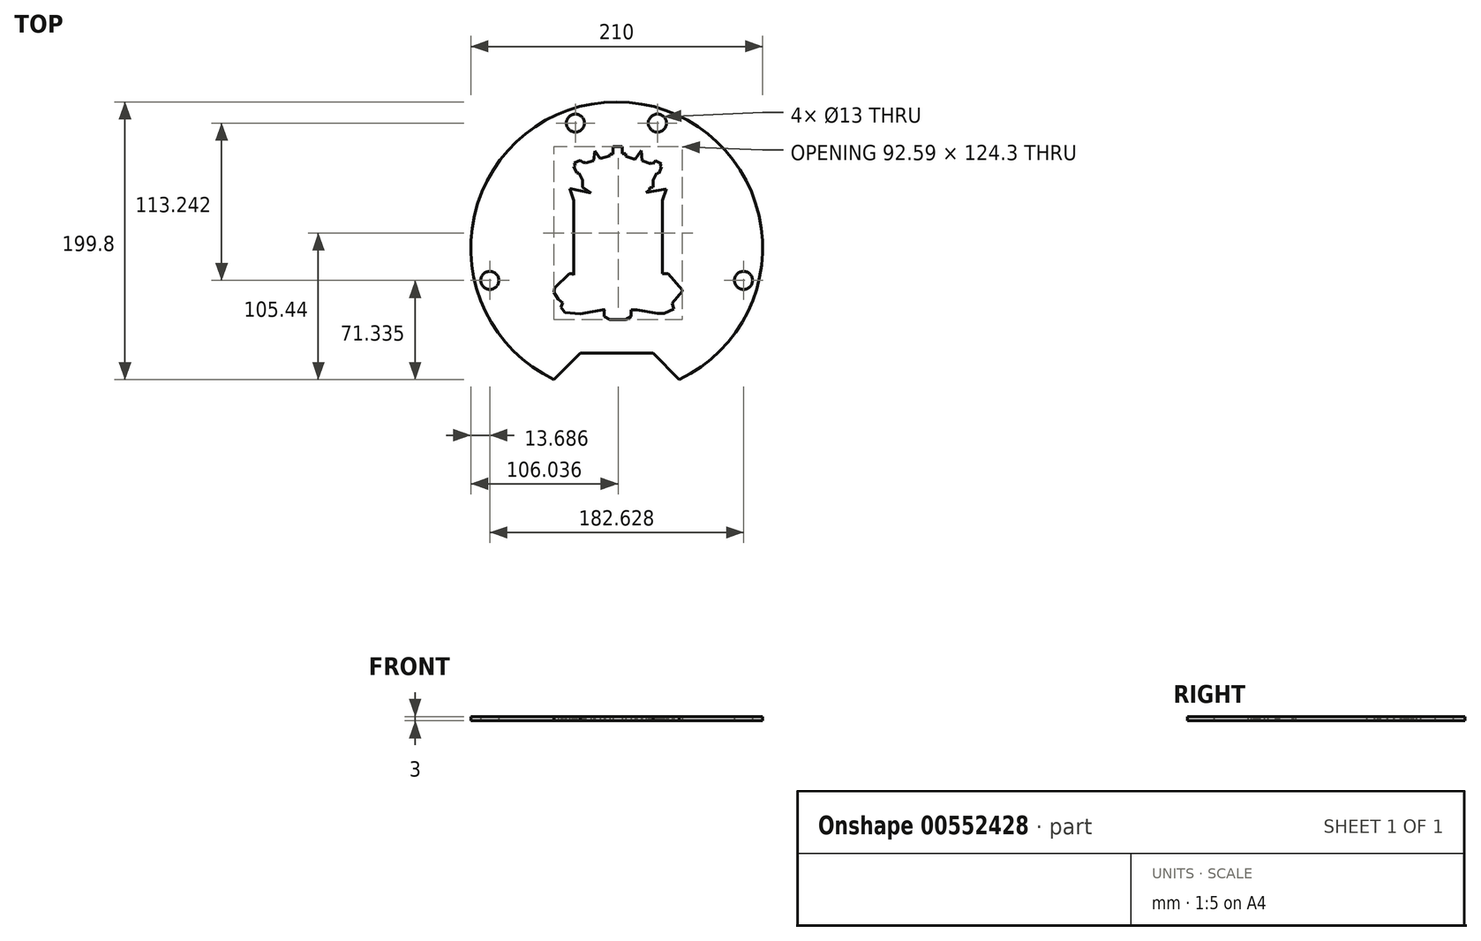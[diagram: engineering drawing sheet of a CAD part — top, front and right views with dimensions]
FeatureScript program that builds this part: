
annotation { "Feature Type Name" : "Feature", "Feature Type Description" : "" }
export const myFeature = defineFeature(function(context is Context, id is Id, definition is map)
    precondition{}
    {
        {
            var Q0;
            Q0=qCreatedBy(makeId("Top.planeOp"),FACE);
            var sketch = newSketch(context, id + "F0", { "sketchPlane" : qUnion([Q0])});
            skCircle(sketch, "E0", {"center": v(0, 0) * mm, "radius": 105 * mm});
            skLineSegment(sketch, "E1", {"start": v(0, 105) * mm, "end": v(0, -105) * mm});
            skLineSegment(sketch, "E2", {"start": v(0, 0) * mm, "end": v(0, 105) * mm});
            skCircle(sketch, "E3", {"center": v(-29.72, 89.78) * mm, "radius": 6.5 * mm});
            skCircle(sketch, "E4", {"center": v(29.3, 89.78) * mm, "radius": 6.5 * mm});
            skCircle(sketch, "E5", {"center": v(-91.31, -23.47) * mm, "radius": 6.5 * mm});
            skCircle(sketch, "E6", {"center": v(91.31, -23.47) * mm, "radius": 6.5 * mm});
            skLineSegment(sketch, "E7", {"start": v(0, -49.67) * mm, "end": v(0, -64.72) * mm});
            skLineSegment(sketch, "E8", {"start": v(-26.12, -75.8) * mm, "end": v(26.12, -75.8) * mm});
            skLineSegment(sketch, "E9", {"start": v(-26.12, -75.8) * mm, "end": v(-45.13, -94.8) * mm});
            skLineSegment(sketch, "E10", {"start": v(26.12, -75.8) * mm, "end": v(45.13, -94.8) * mm});
            skPoint(sketch, "E11.firstSnap0", {"position": v(0, 52.28) * mm});
            skLineSegment(sketch, "E12", {"start": v(-24.45, 48.8) * mm, "end": v(-24.45, 43.76) * mm});
            skLineSegment(sketch, "E13", {"start": v(-24.45, 43.76) * mm, "end": v(-18.38, 39.4) * mm});
            skLineSegment(sketch, "E14", {"start": v(-18.38, 39.4) * mm, "end": v(-33.7, 42.66) * mm});
            skLineSegment(sketch, "E15", {"start": v(-33.7, 42.66) * mm, "end": v(-30.83, 34.09) * mm});
            skLineSegment(sketch, "E16", {"start": v(-30.83, 34.09) * mm, "end": v(-30.83, -19.5) * mm});
            skLineSegment(sketch, "E17", {"start": v(-30.83, -19.5) * mm, "end": v(-32.15, -18.55) * mm});
            skLineSegment(sketch, "E18", {"start": v(-32.15, -18.55) * mm, "end": v(-34.1, -18.55) * mm});
            skLineSegment(sketch, "E19", {"start": v(-34.1, -18.55) * mm, "end": v(-44.57, -28.77) * mm});
            skLineSegment(sketch, "E20", {"start": v(-44.57, -28.77) * mm, "end": v(-45.26, -31.82) * mm});
            skLineSegment(sketch, "E21", {"start": v(-45.26, -31.82) * mm, "end": v(-42.03, -36.93) * mm});
            skLineSegment(sketch, "E22", {"start": v(-42.03, -36.93) * mm, "end": v(-38.78, -39.66) * mm});
            skLineSegment(sketch, "E23", {"start": v(-38.78, -39.66) * mm, "end": v(-40.24, -42.71) * mm});
            skLineSegment(sketch, "E24", {"start": v(-40.24, -42.71) * mm, "end": v(-37.19, -46.5) * mm});
            skLineSegment(sketch, "E25", {"start": v(-37.19, -46.5) * mm, "end": v(-26.16, -47.52) * mm});
            skLineSegment(sketch, "E26", {"start": v(-26.16, -47.52) * mm, "end": v(-8.32, -44.46) * mm});
            skLineSegment(sketch, "E27", {"start": v(-8.32, -44.46) * mm, "end": v(-8.98, -45.38) * mm});
            skLineSegment(sketch, "E28", {"start": v(-8.98, -45.38) * mm, "end": v(-8.98, -49.27) * mm});
            skLineSegment(sketch, "E29", {"start": v(-8.98, -49.27) * mm, "end": v(-4.9, -51.5) * mm});
            skLineSegment(sketch, "E30", {"start": v(-4.9, -51.5) * mm, "end": v(6.5, -51.5) * mm});
            skLineSegment(sketch, "E31", {"start": v(6.5, -51.5) * mm, "end": v(10.4, -49.27) * mm});
            skLineSegment(sketch, "E32", {"start": v(10.4, -49.27) * mm, "end": v(10.4, -44.79) * mm});
            skLineSegment(sketch, "E33", {"start": v(10.4, -44.79) * mm, "end": v(14.56, -44.79) * mm});
            skLineSegment(sketch, "E34", {"start": v(14.56, -44.79) * mm, "end": v(29.34, -47.07) * mm});
            skLineSegment(sketch, "E35", {"start": v(29.34, -47.07) * mm, "end": v(34.1, -47.07) * mm});
            skLineSegment(sketch, "E36", {"start": v(34.1, -47.07) * mm, "end": v(41.06, -43.98) * mm});
            skLineSegment(sketch, "E37", {"start": v(41.06, -43.98) * mm, "end": v(39.92, -39.74) * mm});
            skLineSegment(sketch, "E38", {"start": v(39.92, -39.74) * mm, "end": v(47.33, -31.23) * mm});
            skLineSegment(sketch, "E39", {"start": v(47.33, -31.23) * mm, "end": v(47.33, -30.38) * mm});
            skLineSegment(sketch, "E40", {"start": v(47.33, -30.38) * mm, "end": v(37, -18.55) * mm});
            skLineSegment(sketch, "E41", {"start": v(37, -18.55) * mm, "end": v(32.96, -18.55) * mm});
            skLineSegment(sketch, "E42", {"start": v(32.96, -18.55) * mm, "end": v(32.96, -17.68) * mm});
            skLineSegment(sketch, "E43", {"start": v(32.96, 34.09) * mm, "end": v(35.77, 42.38) * mm});
            skLineSegment(sketch, "E44", {"start": v(35.77, 42.38) * mm, "end": v(21.07, 39.81) * mm});
            skLineSegment(sketch, "E45", {"start": v(21.07, 39.81) * mm, "end": v(23.84, 41.77) * mm});
            skLineSegment(sketch, "E46", {"start": v(23.84, 41.77) * mm, "end": v(23.84, 43.15) * mm});
            skLineSegment(sketch, "E47", {"start": v(23.84, 43.15) * mm, "end": v(26.2, 43.76) * mm});
            skLineSegment(sketch, "E48", {"start": v(26.2, 43.76) * mm, "end": v(26.2, 48.85) * mm});
            skLineSegment(sketch, "E49", {"start": v(26.2, 48.85) * mm, "end": v(28.8, 53.86) * mm});
            skLineSegment(sketch, "E50", {"start": v(28.8, 53.86) * mm, "end": v(30.3, 53.52) * mm});
            skLineSegment(sketch, "E51", {"start": v(30.3, 53.52) * mm, "end": v(32.19, 58.3) * mm});
            skLineSegment(sketch, "E52", {"start": v(32.19, 58.3) * mm, "end": v(31.01, 58.76) * mm});
            skLineSegment(sketch, "E53", {"start": v(31.01, 58.76) * mm, "end": v(32.31, 60.57) * mm});
            skLineSegment(sketch, "E54", {"start": v(32.31, 60.57) * mm, "end": v(27.87, 62.7) * mm});
            skLineSegment(sketch, "E55", {"start": v(27.87, 62.7) * mm, "end": v(26.34, 60.57) * mm});
            skLineSegment(sketch, "E56", {"start": v(26.34, 60.57) * mm, "end": v(25.25, 61.35) * mm});
            skLineSegment(sketch, "E57", {"start": v(25.25, 61.35) * mm, "end": v(24.7, 60.57) * mm});
            skLineSegment(sketch, "E58", {"start": v(24.7, 60.57) * mm, "end": v(18.22, 62.53) * mm});
            skLineSegment(sketch, "E59", {"start": v(18.22, 62.53) * mm, "end": v(17.77, 70.06) * mm});
            skLineSegment(sketch, "E60", {"start": v(17.77, 70.06) * mm, "end": v(13.24, 63.75) * mm});
            skLineSegment(sketch, "E61", {"start": v(13.24, 63.75) * mm, "end": v(6.42, 65.79) * mm});
            skLineSegment(sketch, "E62", {"start": v(6.42, 65.79) * mm, "end": v(6.42, 67.82) * mm});
            skLineSegment(sketch, "E63", {"start": v(6.42, 67.82) * mm, "end": v(4.14, 67.82) * mm});
            skLineSegment(sketch, "E64", {"start": v(4.14, 67.82) * mm, "end": v(4.14, 72.79) * mm});
            skLineSegment(sketch, "E65", {"start": v(4.14, 72.79) * mm, "end": v(-2.5, 72.79) * mm});
            skLineSegment(sketch, "E66", {"start": v(-2.5, 72.79) * mm, "end": v(-2.5, 67.54) * mm});
            skLineSegment(sketch, "E67", {"start": v(-2.5, 67.54) * mm, "end": v(-4.9, 67.54) * mm});
            skLineSegment(sketch, "E68", {"start": v(-4.9, 67.54) * mm, "end": v(-4.9, 66.03) * mm});
            skLineSegment(sketch, "E69", {"start": v(-4.9, 66.03) * mm, "end": v(-11.86, 64.2) * mm});
            skLineSegment(sketch, "E70", {"start": v(-11.86, 64.2) * mm, "end": v(-15.73, 69.5) * mm});
            skLineSegment(sketch, "E71", {"start": v(-15.73, 69.5) * mm, "end": v(-16.7, 62.53) * mm});
            skLineSegment(sketch, "E72", {"start": v(-16.7, 62.53) * mm, "end": v(-22.42, 61.03) * mm});
            skLineSegment(sketch, "E73", {"start": v(-22.42, 61.03) * mm, "end": v(-22.97, 61.42) * mm});
            skLineSegment(sketch, "E74", {"start": v(-22.97, 61.42) * mm, "end": v(-24.08, 61.42) * mm});
            skLineSegment(sketch, "E75", {"start": v(-24.08, 61.42) * mm, "end": v(-26.28, 63) * mm});
            skLineSegment(sketch, "E76", {"start": v(-26.28, 63) * mm, "end": v(-30.43, 61.03) * mm});
            skLineSegment(sketch, "E77", {"start": v(-30.43, 61.03) * mm, "end": v(-29.48, 59.03) * mm});
            skLineSegment(sketch, "E78", {"start": v(-29.48, 59.03) * mm, "end": v(-30.83, 58.4) * mm});
            skLineSegment(sketch, "E79", {"start": v(-30.83, 58.4) * mm, "end": v(-28.6, 53.71) * mm});
            skLineSegment(sketch, "E80", {"start": v(-28.6, 53.71) * mm, "end": v(-26.97, 53.71) * mm});
            skLineSegment(sketch, "E81", {"start": v(-26.97, 53.71) * mm, "end": v(-24.45, 48.8) * mm});
            skLineSegment(sketch, "E82", {"start": v(0.73, 42.14) * mm, "end": v(-4, 29.48) * mm});
            skLineSegment(sketch, "E83", {"start": v(-4, 29.48) * mm, "end": v(-18.96, 29.48) * mm});
            skLineSegment(sketch, "E84", {"start": v(-18.96, 29.48) * mm, "end": v(-7.05, 21.42) * mm});
            skLineSegment(sketch, "E85", {"start": v(-7.05, 21.42) * mm, "end": v(-12.69, 8.46) * mm});
            skLineSegment(sketch, "E86", {"start": v(-12.69, 8.46) * mm, "end": v(-9.69, 10) * mm});
            skLineSegment(sketch, "E87", {"start": v(-9.69, 10) * mm, "end": v(-10.9, 6.68) * mm});
            skLineSegment(sketch, "E88", {"start": v(-10.9, 6.68) * mm, "end": v(-28.3, 6.68) * mm});
            skLineSegment(sketch, "E89", {"start": v(-28.3, 6.68) * mm, "end": v(-28.3, 35) * mm});
            skLineSegment(sketch, "E90", {"start": v(-28.3, 35) * mm, "end": v(-30.42, 39.15) * mm});
            skLineSegment(sketch, "E91", {"start": v(-30.42, 39.15) * mm, "end": v(-22.13, 37.25) * mm});
            skLineSegment(sketch, "E92", {"start": v(-22.13, 37.25) * mm, "end": v(-12.63, 37.25) * mm});
            skLineSegment(sketch, "E93", {"start": v(-12.63, 37.25) * mm, "end": v(-4.85, 39.3) * mm});
            skLineSegment(sketch, "E94", {"start": v(-4.85, 39.3) * mm, "end": v(0.73, 42.14) * mm});
            skLineSegment(sketch, "E95", {"start": v(0.73, 42.14) * mm, "end": v(5.74, 39.5) * mm});
            skLineSegment(sketch, "E96", {"start": v(5.74, 39.5) * mm, "end": v(9.94, 37.93) * mm});
            skLineSegment(sketch, "E97", {"start": v(9.94, 37.93) * mm, "end": v(14.03, 36.96) * mm});
            skLineSegment(sketch, "E98", {"start": v(14.03, 36.96) * mm, "end": v(23.93, 36.96) * mm});
            skLineSegment(sketch, "E99", {"start": v(23.93, 36.96) * mm, "end": v(32.17, 39.72) * mm});
            skLineSegment(sketch, "E100", {"start": v(32.17, 39.72) * mm, "end": v(29.86, 35) * mm});
            skLineSegment(sketch, "E101", {"start": v(29.86, 35) * mm, "end": v(29.86, 6.68) * mm});
            skLineSegment(sketch, "E102", {"start": v(29.86, 6.68) * mm, "end": v(12.8, 6.68) * mm});
            skLineSegment(sketch, "E103", {"start": v(12.8, 6.68) * mm, "end": v(11.7, 10) * mm});
            skLineSegment(sketch, "E104", {"start": v(11.7, 10) * mm, "end": v(14.27, 8.22) * mm});
            skLineSegment(sketch, "E105", {"start": v(14.27, 8.22) * mm, "end": v(8.82, 21.57) * mm});
            skLineSegment(sketch, "E106", {"start": v(8.82, 21.57) * mm, "end": v(20.54, 29.14) * mm});
            skLineSegment(sketch, "E107", {"start": v(20.54, 29.14) * mm, "end": v(5.72, 29.14) * mm});
            skLineSegment(sketch, "E108", {"start": v(5.72, 29.14) * mm, "end": v(0.73, 42.14) * mm});
            skLineSegment(sketch, "E109", {"start": v(7.52, 12.37) * mm, "end": v(8.09, 6.68) * mm});
            skLineSegment(sketch, "E110", {"start": v(8.09, 6.68) * mm, "end": v(9.94, 6.68) * mm});
            skLineSegment(sketch, "E111", {"start": v(9.94, 6.68) * mm, "end": v(9.23, 11.1) * mm});
            skLineSegment(sketch, "E112", {"start": v(9.23, 11.1) * mm, "end": v(7.52, 12.37) * mm});
            skLineSegment(sketch, "E113", {"start": v(3.94, 14.93) * mm, "end": v(5.04, 14) * mm});
            skLineSegment(sketch, "E114", {"start": v(5.04, 14) * mm, "end": v(5.77, 6.68) * mm});
            skLineSegment(sketch, "E115", {"start": v(5.77, 6.68) * mm, "end": v(4.36, 6.53) * mm});
            skLineSegment(sketch, "E116", {"start": v(4.36, 6.53) * mm, "end": v(3.94, 14.93) * mm});
            skLineSegment(sketch, "E117", {"start": v(0.73, 16.6) * mm, "end": v(1.43, 16.34) * mm});
            skLineSegment(sketch, "E118", {"start": v(1.43, 16.34) * mm, "end": v(1.9, 6.68) * mm});
            skLineSegment(sketch, "E119", {"start": v(1.9, 6.68) * mm, "end": v(0.42, 6.53) * mm});
            skLineSegment(sketch, "E120", {"start": v(0.42, 6.53) * mm, "end": v(0.73, 16.6) * mm});
            skLineSegment(sketch, "E121", {"start": v(-2.66, 14.48) * mm, "end": v(-1.78, 14.93) * mm});
            skLineSegment(sketch, "E122", {"start": v(-1.78, 14.93) * mm, "end": v(-2.2, 6.68) * mm});
            skLineSegment(sketch, "E123", {"start": v(-2.2, 6.68) * mm, "end": v(-3.66, 6.75) * mm});
            skLineSegment(sketch, "E124", {"start": v(-3.66, 6.75) * mm, "end": v(-2.66, 14.48) * mm});
            skLineSegment(sketch, "E125", {"start": v(-6.69, 11.92) * mm, "end": v(-5.2, 12.68) * mm});
            skLineSegment(sketch, "E126", {"start": v(-5.2, 12.68) * mm, "end": v(-6.56, 6.68) * mm});
            skLineSegment(sketch, "E127", {"start": v(-6.56, 6.68) * mm, "end": v(-8.15, 6.68) * mm});
            skLineSegment(sketch, "E128", {"start": v(-8.15, 6.68) * mm, "end": v(-6.69, 11.92) * mm});
            skLineSegment(sketch, "E129", {"start": v(-28.4, -6.14) * mm, "end": v(-15.15, -6.14) * mm});
            skLineSegment(sketch, "E130", {"start": v(-15.15, -6.14) * mm, "end": v(-21.72, -27.22) * mm});
            skLineSegment(sketch, "E131", {"start": v(-21.72, -27.22) * mm, "end": v(-26.44, -23.3) * mm});
            skLineSegment(sketch, "E132", {"start": v(-26.44, -23.3) * mm, "end": v(-28.25, -19.78) * mm});
            skLineSegment(sketch, "E133", {"start": v(-28.25, -19.78) * mm, "end": v(-28.25, -16.05) * mm});
            skLineSegment(sketch, "E134", {"start": v(-28.25, -16.05) * mm, "end": v(-28.65, -15.26) * mm});
            skLineSegment(sketch, "E135", {"start": v(-28.65, -15.26) * mm, "end": v(-28.4, -6.14) * mm});
            skLineSegment(sketch, "E136", {"start": v(-11.35, -6.14) * mm, "end": v(-9.05, -5.91) * mm});
            skLineSegment(sketch, "E137", {"start": v(-9.05, -5.91) * mm, "end": v(-13.42, -27.68) * mm});
            skLineSegment(sketch, "E138", {"start": v(-13.42, -27.68) * mm, "end": v(-16.53, -27.99) * mm});
            skLineSegment(sketch, "E139", {"start": v(-16.53, -27.99) * mm, "end": v(-11.35, -6.14) * mm});
            skLineSegment(sketch, "E140", {"start": v(-5.36, -6.14) * mm, "end": v(-3.15, -5.92) * mm});
            skLineSegment(sketch, "E141", {"start": v(-3.15, -5.92) * mm, "end": v(-5.36, -29.86) * mm});
            skLineSegment(sketch, "E142", {"start": v(-5.36, -29.86) * mm, "end": v(-8.51, -28.71) * mm});
            skLineSegment(sketch, "E143", {"start": v(-8.51, -28.71) * mm, "end": v(-5.36, -6.14) * mm});
            skLineSegment(sketch, "E144", {"start": v(0, -6.14) * mm, "end": v(2.27, -5.92) * mm});
            skLineSegment(sketch, "E145", {"start": v(2.27, -5.92) * mm, "end": v(2.27, -32.74) * mm});
            skLineSegment(sketch, "E146", {"start": v(2.27, -32.74) * mm, "end": v(0.91, -34.64) * mm});
            skLineSegment(sketch, "E147", {"start": v(0.91, -34.64) * mm, "end": v(-0.41, -33.3) * mm});
            skLineSegment(sketch, "E148", {"start": v(-0.41, -33.3) * mm, "end": v(0, -6.14) * mm});
            skLineSegment(sketch, "E149", {"start": v(5.5, -6.14) * mm, "end": v(7.46, -6.14) * mm});
            skLineSegment(sketch, "E150", {"start": v(7.46, -6.14) * mm, "end": v(10.8, -29.07) * mm});
            skLineSegment(sketch, "E151", {"start": v(10.8, -29.07) * mm, "end": v(7.6, -29.54) * mm});
            skLineSegment(sketch, "E152", {"start": v(7.6, -29.54) * mm, "end": v(5.5, -6.14) * mm});
            skLineSegment(sketch, "E153", {"start": v(11.53, -6.14) * mm, "end": v(12.83, -6.14) * mm});
            skLineSegment(sketch, "E154", {"start": v(12.83, -6.14) * mm, "end": v(18.61, -27.85) * mm});
            skLineSegment(sketch, "E155", {"start": v(18.61, -27.85) * mm, "end": v(15.68, -27.85) * mm});
            skLineSegment(sketch, "E156", {"start": v(15.68, -27.85) * mm, "end": v(11.53, -6.14) * mm});
            skLineSegment(sketch, "E157", {"start": v(17.23, -6.14) * mm, "end": v(23.82, -26.8) * mm});
            skLineSegment(sketch, "E158", {"start": v(23.82, -26.8) * mm, "end": v(28.8, -22.24) * mm});
            skLineSegment(sketch, "E159", {"start": v(28.8, -22.24) * mm, "end": v(29.9, -19.2) * mm});
            skLineSegment(sketch, "E160", {"start": v(29.9, -19.2) * mm, "end": v(29.9, -5.92) * mm});
            skLineSegment(sketch, "E161", {"start": v(29.9, -5.92) * mm, "end": v(17.23, -6.14) * mm});
            skLineSegment(sketch, "E162", {"start": v(32.96, 34.09) * mm, "end": v(32.96, -17.68) * mm});
            skSolve(sketch);
        }
        {
            var Q0;
            Q0=makeQuery(id+"F0.imprint","IMPRINT",FACE,{"disambiguationData":[TD([[makeQuery(id+"F0.imprint","IMPRINT",EDGE,{"derivedFrom":sQuery(id+"F0.wireOp",EDGE,"E3")}),-1.0]])]});
            var Q1;
            Q1=makeQuery(id+"F0.imprint","IMPRINT",FACE,{"disambiguationData":[TD([[makeQuery(id+"F0.imprint","IMPRINT",EDGE,{"derivedFrom":sQuery(id+"F0.wireOp",EDGE,"E4")}),-1.0]])]});
            extrude(context, id + "F1", {"entities" : qUnion([Q0, Q1]), "depth" : 3 * mm, "offsetDistance" : 25.4 * mm});
        }
    });
